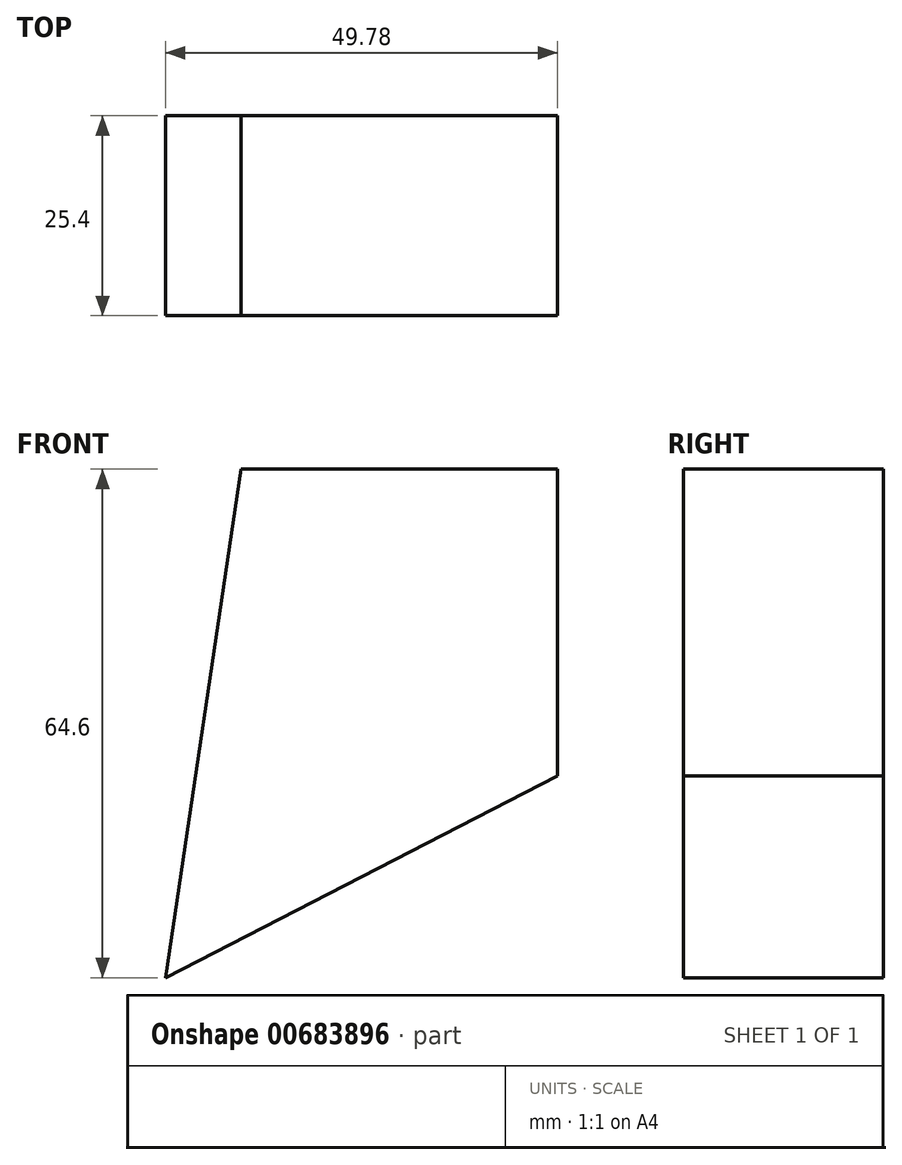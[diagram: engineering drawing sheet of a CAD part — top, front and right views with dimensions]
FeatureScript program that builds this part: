
annotation { "Feature Type Name" : "Feature", "Feature Type Description" : "" }
export const myFeature = defineFeature(function(context is Context, id is Id, definition is map)
    precondition{}
    {
        {
            var Q0;
            Q0=qCreatedBy(makeId("Front.planeOp"),FACE);
            var sketch = newSketch(context, id + "F0", { "sketchPlane" : qUnion([Q0])});
            skLineSegment(sketch, "E0", {"start": v(0, 38.96) * mm, "end": v(40.22, 38.96) * mm});
            skLineSegment(sketch, "E1", {"start": v(40.22, 38.96) * mm, "end": v(40.22, 0) * mm});
            skLineSegment(sketch, "E2", {"start": v(40.22, 0) * mm, "end": v(-9.56, -25.64) * mm});
            skLineSegment(sketch, "E3", {"start": v(-9.56, -25.64) * mm, "end": v(0, 38.96) * mm});
            skSolve(sketch);
        }
        {
            var Q0;
            Q0=makeQuery(id+"F0.imprint","IMPRINT",FACE,{"disambiguationData":[TD([[makeQuery(id+"F0.imprint","IMPRINT",EDGE,{"derivedFrom":sQuery(id+"F0.wireOp",EDGE,"E0")}),-1.0]])]});
            extrude(context, id + "F1", {"entities" : qUnion([Q0]), "depth" : 25.4 * mm, "offsetDistance" : 25.4 * mm});
        }
        {
            var Q0;
            Q0=makeQuery(id+"F1.opExtrude","CAP_FACE",FACE,{"disambiguationData":[OSD([sQuery(id+"F0.wireOp",EDGE,"E0"),sQuery(id+"F0.wireOp",EDGE,"E1"),sQuery(id+"F0.wireOp",EDGE,"E2"),sQuery(id+"F0.wireOp",EDGE,"E3")])],"isStart":true});
            var sketch = newSketch(context, id + "F2", { "sketchPlane" : qUnion([Q0])});
            skSolve(sketch);
        }
        {
            var Q0;
            Q0=makeQuery(id+"F2.imprint","IMPRINT",FACE,{"disambiguationData":[TD([[makeQuery(id+"F2.imprint","IMPRINT",EDGE,{"derivedFrom":makeQuery(id+"F1.opExtrude","CAP_EDGE",EDGE,{"disambiguationData":[OSD([sQuery(id+"F0.wireOp",EDGE,"E0")])],"isStart":true})}),1.0]])]});
            var sketch = newSketch(context, id + "F3", { "sketchPlane" : qUnion([Q0])});
            skEllipse(sketch, "E4", {"center": v(-15.77, 15.14) * mm, "majorRadius": 20.86 * mm, "minorRadius": 2.83 * mm, "majorAxis": v(-0.43, 0.9)});
            skSolve(sketch);
        }
        {
            var Q0;
            Q0=sQuery(id+"F3.wireOp",EDGE,"E4");
            extrude(context, id + "F4", {"bodyType" : ToolBodyType.SURFACE, "surfaceEntities" : qUnion([Q0]), "depth" : 25.4 * mm, "offsetDistance" : 25.4 * mm});
        }
    });
